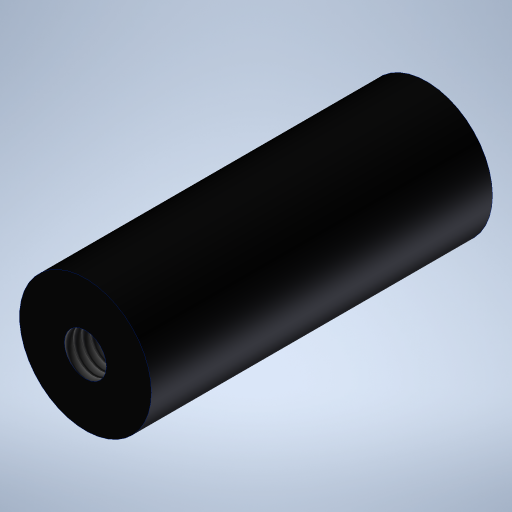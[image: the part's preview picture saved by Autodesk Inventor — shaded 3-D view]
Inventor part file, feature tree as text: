
AUTODESK INVENTOR PART (.ipt)
format: ipt  version: 2024 (Build 280153000, 153)  size: 215,040 bytes
history: native  units: in
note: dims shown in document units (in); Inventor stores cm internally (conversion verified against a paired STEP export)
features: extrude x1, thread x1, sketch x1
ambient origin geometry x8: Origin, YZ Plane, XZ Plane, XY Plane, X Axis, Y Axis, Z Axis, Center Point
bodies: Solid1 (feature_tree)
feature tree (3):
  extrude  "Extrusion1"  Depth=1.293in
  thread  "Thread1"  [1 undecoded]
  sketch  "Sketch1"  dims[d0=0.159in d1=0.5in d2=1.293in d3=0.0in d4=1.293in d5=0.0in]
note: 1 required parameter value undecoded (feature->parameter linkage not recoverable at this tier; creation-order binding heuristic only, values carry confidence <= 0.55)
